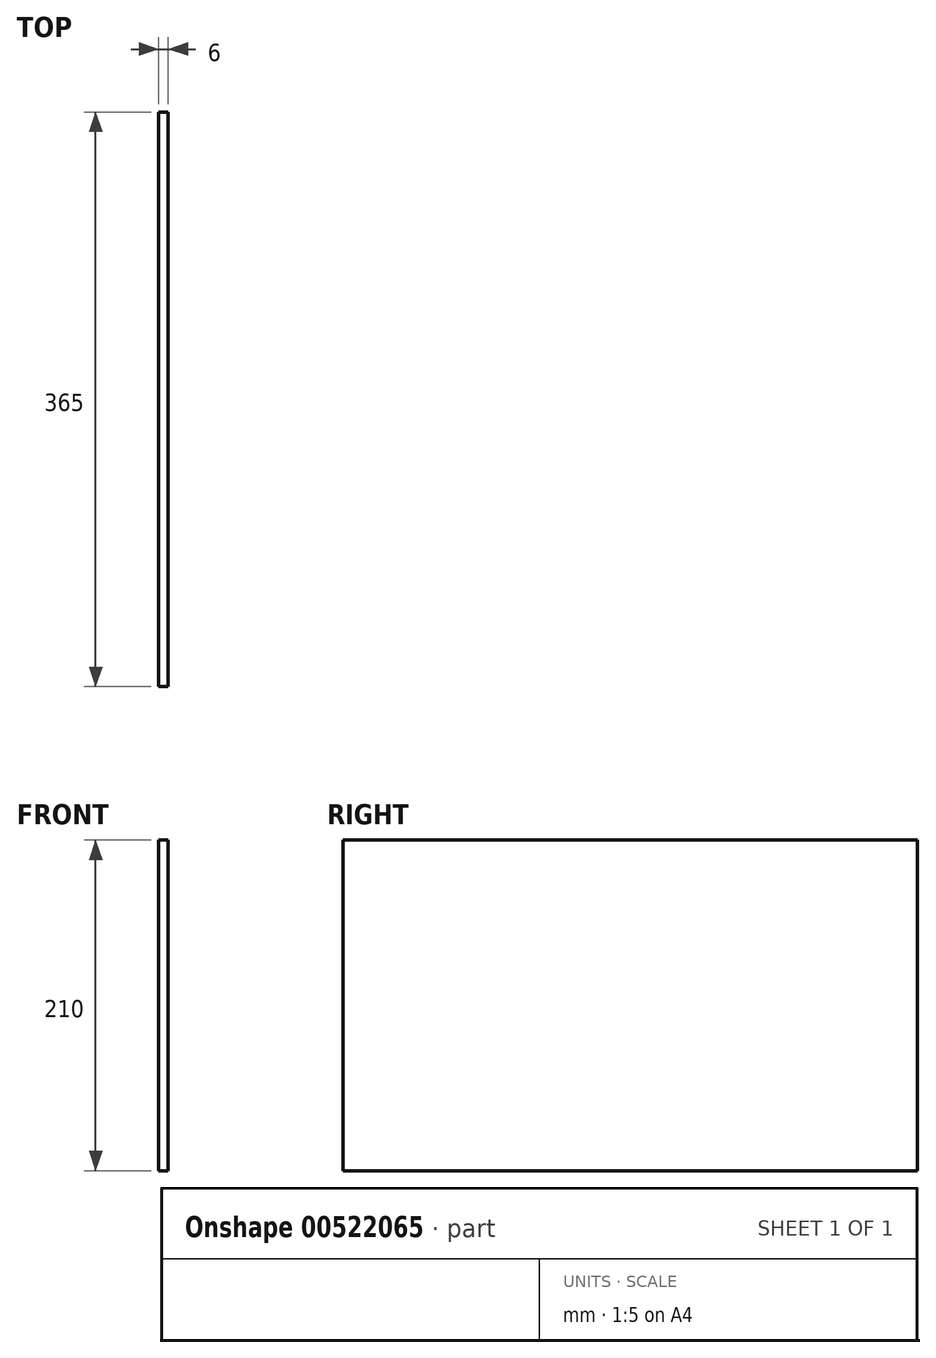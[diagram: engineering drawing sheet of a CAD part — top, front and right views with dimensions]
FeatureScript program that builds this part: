
annotation { "Feature Type Name" : "Feature", "Feature Type Description" : "" }
export const myFeature = defineFeature(function(context is Context, id is Id, definition is map)
    precondition{}
    {
        {
            var Q0;
            Q0=qCreatedBy(makeId("Right.planeOp"),FACE);
            var sketch = newSketch(context, id + "F0", { "sketchPlane" : qUnion([Q0])});
            skLineSegment(sketch, "E0.bottom", {"start": v(0, 0) * mm, "end": v(365, 0) * mm});
            skLineSegment(sketch, "E0.top", {"start": v(0, 210) * mm, "end": v(365, 210) * mm});
            skLineSegment(sketch, "E0.left", {"start": v(0, 0) * mm, "end": v(0, 210) * mm});
            skLineSegment(sketch, "E0.right", {"start": v(365, 0) * mm, "end": v(365, 210) * mm});
            skSolve(sketch);
        }
        {
            var Q0;
            Q0=makeQuery(id+"F0.imprint","IMPRINT",FACE,{"disambiguationData":[TD([[makeQuery(id+"F0.imprint","IMPRINT",EDGE,{"derivedFrom":sQuery(id+"F0.wireOp",EDGE,"E0.bottom")}),1.0]])]});
            extrude(context, id + "F1", {"entities" : qUnion([Q0]), "oppositeDirection" : true, "depth" : 6 * mm, "offsetDistance" : 25 * mm});
        }
    });
